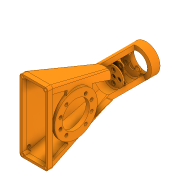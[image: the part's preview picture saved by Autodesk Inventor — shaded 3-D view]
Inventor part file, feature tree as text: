
AUTODESK INVENTOR PART (.ipt)
format: ipt  version: 2020 (Build 240168000, 168)  size: 1,528,832 bytes
history: native  units: in
note: dims shown in document units (in); Inventor stores cm internally (conversion verified against a paired STEP export)
features: sketch x28, extrude x24, projected_geometry x14, chamfer x4, fillet x4, plane x3, loft x2, other x1
ambient origin geometry x8: Origin, YZ Plane, XZ Plane, XY Plane, X Axis, Y Axis, Z Axis, Center Point
bodies: Solid1 (feature_tree)
feature tree (80):
  extrude  "Extrusion1"  Depth=2.0472in
  extrude  "Extrusion2"  Depth=1.6535in
  chamfer  "Chamfer1"  Distance=0.5512in
  extrude  "Extrusion3"  Depth=0.0157in
  extrude  "Extrusion4"  Depth=0.2756in TaperAngle=0.0deg
  extrude  "Extrusion5"  Depth=0.315in
  extrude  "Extrusion6"  Depth=0.4724in
  extrude  "Extrusion7"  Depth=0.0787in
  plane  "Work Plane1"
  sketch  "Sketch9"  dims[d26=0.0984in d27=0.0in d28=0.1575in]
  plane  "Work Plane2"
  extrude  "Extrusion9"  Depth=0.1575in
  sketch  "Sketch11"  dims[d31=15.0deg d32=0.4921in d33=0.0in]
  plane  "Work Plane3"
  extrude  "Extrusion10"  Depth=1.0994in
  extrude  "Extrusion11"  Depth=0.4921in TaperAngle=0.0deg
  loft  "Loft1"
  loft  "Loft2"
  sketch  "Sketch16"  dims[d47=0.315in d48=0.4331in]
  extrude  "Extrusion12"  Depth=0.0787in
  extrude  "Extrusion13"  Depth=0.0984in TaperAngle=0.0deg
  extrude  "Extrusion14"  Depth=0.4331in
  extrude  "Extrusion15"  Depth=0.1575in
  fillet  "Fillet1"  Radius=0.1575in
  chamfer  "Chamfer23"  Distance=0.0984in
  extrude  "Extrusion19"  Depth=0.8858in
  extrude  "Extrusion20"  Depth=1.6654in
  extrude  "Extrusion21"  TaperAngle=0.0deg  [1 undecoded]
  extrude  "Extrusion22"  Depth=1.6654in
  extrude  "Extrusion23"  Depth=0.1969in
  extrude  "Extrusion24"  Depth=0.3484in
  extrude  "Extrusion25"  Depth=0.1969in
  chamfer  "Chamfer24"  Distance=0.3937in
  extrude  "Extrusion26"  TaperAngle=0.0deg  [1 undecoded]
  fillet  "Fillet2"  [1 undecoded]
  extrude  "Extrusion27"  TaperAngle=0.0deg  [1 undecoded]
  chamfer  "Chamfer25"  Distance=0.7874in
  extrude  "Extrusion28"  Depth=0.3937in
  fillet  "Fillet4"  Radius=0.7874in
  fillet  "Fillet5"  Radius=0.1969in
  sketch  "Sketch1"  dims[d0=2.3622in d1=2.0472in]
  sketch  "Sketch2"  dims[d2=0.5591in d3=0.0in d4=1.6535in d5=0.5512in d6=0.0in]
  sketch  "Sketch3"  dims[d7=0.5591in d8=0.125in d9=0.0137in d10=0.0157in]
  sketch  "Sketch5"  dims[d11=4.7244in d13=360.0deg d15=0.2756in d16=0.0in]
  sketch  "Sketch6"  dims[d17=0.5512in d19=0.315in]
  projected_geometry  "Projected Loop1"
  sketch  "Sketch7"  dims[d20=0.315in d21=0.4724in]
  projected_geometry  "Projected Loop2"
  sketch  "Sketch8"  dims[d22=0.4724in d23=0.0787in d24=0.0787in d25=0.0787in]
  projected_geometry  "Projected Loop3"
  sketch  "Sketch10"  dims[d29=0.1575in d30=1.0994in]
  sketch  "Sketch12"  dims[d34=1.4567in d35=0.0in d36=1.5748in d38=360.0deg]
  sketch  "Sketch13"  dims[d40=0.0787in d41=0.0787in]
  projected_geometry  "Projected Loop4"
  other  "Edges1"
  sketch  "Sketch14"  dims[d42=0.0787in d43=0.0787in]
  projected_geometry  "Projected Loop5"
  sketch  "Sketch15"  dims[d44=0.0787in d45=0.0984in d46=0.0in]
  projected_geometry  "Projected Loop6"
  projected_geometry  "Projected Loop7"
  sketch  "Sketch19"  dims[d51=0.6161in d52=0.1575in d53=0.1575in d54=0.0984in d55=0.0in]
  projected_geometry  "Projected Loop8"
  sketch  "Sketch20"  dims[d56=6.6929in d57=0.8858in]
  projected_geometry  "Projected Loop9"
  sketch  "Sketch21"  dims[d58=1.6654in d59=1.6654in]
  sketch  "Sketch25"  dims[d60=0.0in d61=0.0in]
  sketch  "Sketch26"  dims[d62=1.6654in d63=1.6654in]
  projected_geometry  "Projected Loop11"
  sketch  "Sketch27"  dims[d64=0.1969in d65=0.1969in]
  projected_geometry  "Projected Loop12"
  sketch  "Sketch28"  dims[d66=0.3484in d67=0.3484in]
  sketch  "Sketch29"  dims[d68=0.1969in d69=0.1969in]
  sketch  "Sketch30"  dims[d70=0.1969in d71=0.3937in d72=0.0in]
  sketch  "Sketch31"  dims[d73=0.7874in d74=0.0in d75=0.0in d76=90.0deg d77=0.0in d78=90.0deg]
  projected_geometry  "Projected Loop13"
  sketch  "Sketch32"  dims[d79=0.0in d80=90.0deg d81=0.0in d82=90.0deg d86=0.7874in d87=0.0in]
  projected_geometry  "Projected Loop14"
  sketch  "Sketch33"  dims[d90=0.3937in d91=0.3937in d92=0.7874in d93=0.0in d94=0.1969in d95=0.0in]
  projected_geometry  "Projected Loop15"
  sketch  "Sketch34"  dims[d96=0.8858in d97=1.6654in d98=1.6654in d99=0.0in d100=0.0in d101=0.2224in d102=0.1575in d103=0.1575in d104=0.1575in d105=0.1575in d106=0.0984in d107=0.0984in d108=0.1969in d109=0.0in d185=0.0315in d193=0.0984in d194=0.3937in d195=0.125in d196=45.0deg d197=0.2756in d198=0.1969in d199=0.0in d200=0.2756in d201=2.7559in d202=0.2756in d203=0.2756in d204=0.2756in d205=0.2756in d206=0.2756in d207=0.2756in d208=0.2756in d209=0.0394in d210=0.2047in d211=0.0in d212=0.1969in d213=0.2756in d214=0.0in d215=1.0in d216=0.0in d217=0.2362in d218=0.2362in d219=0.2362in d220=0.2362in d221=0.2362in d222=0.0in d223=0.3937in d224=0.0in d225=0.1575in d226=0.0in d227=0.315in d228=0.187in d229=0.125in d230=45.0deg d231=1.0in d232=0.0in d233=0.1969in d235=0.4724in d236=0.0984in d237=0.0in d238=0.0984in d239=0.125in d240=45.0deg d241=0.4724in d243=0.4724in d244=0.4331in d245=0.4724in d247=0.1181in d248=0.0984in d249=0.0in d250=0.0315in d251=0.0394in]
note: 4 required parameter values undecoded (feature->parameter linkage not recoverable at this tier; creation-order binding heuristic only, values carry confidence <= 0.55)
